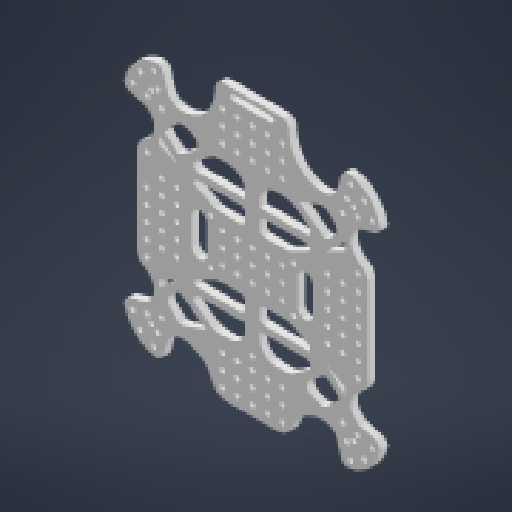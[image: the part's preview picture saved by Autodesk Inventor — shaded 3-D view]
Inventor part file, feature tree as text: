
AUTODESK INVENTOR PART (.ipt)
format: ipt  version: 2023 (Build 270158000, 158)  size: 962,048 bytes
history: native  units: mm
features: fillet x10, other x9, extrude x7, sketch x5, reference x4
ambient origin geometry x8: Origin, YZ Plane, XZ Plane, XY Plane, X Axis, Y Axis, Z Axis, Center Point
bodies: Solid1 (feature_tree)
feature tree (35):
  other  "Base Sketch With Dimensions"
  extrude  "Extrusion1"  TaperAngle=30.0deg  [1 undecoded]
  fillet  "Fillet1"  [1 undecoded]
  sketch  "Sketch3"  dims[d0=3.5mm d1=30.0deg d2=30.0deg]
  extrude  "Side Extensions"  TaperAngle=30.0deg  [1 undecoded]
  extrude  "Bottom Holes"  TaperAngle=30.0deg  [1 undecoded]
  fillet  "Fillet2"  Radius=45.0mm
  extrude  "ESC holders"  Depth=25.0mm
  extrude  "Hole Countersinks"  TaperAngle=135.0deg  [1 undecoded]
  extrude  "Skeleton"  TaperAngle=135.0deg  [1 undecoded]
  fillet  "Fillet3"  Radius=20.0mm
  fillet  "Fillet4"  Radius=120.0mm
  fillet  "Fillet5"  Radius=120.0mm
  fillet  "Fillet6"  Radius=25.0mm
  fillet  "Fillet8"  Radius=5.0mm
  fillet  "Fillet9"  Radius=5.0mm
  fillet  "Fillet10"  Radius=10.0mm
  fillet  "Fillet11"  Radius=10.0mm
  extrude  "Extrusion9"  Depth=10.0mm
  reference  "Reference1"
  reference  "Reference2"
  reference  "Reference3"
  reference  "Reference4"
  sketch  "Sketch4"  dims[d3=20.0mm d5=30.0deg d6=30.0deg]
  other  "Skeleton Sketch"
  sketch  "Sketch6"  dims[d9=30.0deg d10=30.0deg d13=30.0deg d14=30.0deg d16=45.0mm]
  sketch  "Sketch7"  dims[d17=140.0mm d18=25.0mm]
  sketch  "Sketch8"  dims[d19=70.0mm d23=135.0deg d25=135.0deg d29=20.0mm d30=120.0mm d32=120.0mm d40=25.0mm d41=5.0mm d44=5.0mm d45=0.0mm d46=10.0mm d80=50.0mm d82=10.0mm d83=30.0mm d85=10.0mm d88=50.0mm d90=10.0mm d91=30.0mm d93=10.0mm d97=5.0mm d98=50.0mm d102=10.0mm d103=0.0mm d104=17.5mm d105=0.0mm d106=70.0mm d107=10.0mm d108=50.0mm d109=30.0mm d134=3.5mm d135=0.5mm d136=0.5mm d137=30.0mm d138=30.0mm d139=25.0mm d140=0.0mm d151=6.5mm d152=50.0mm d154=10.0mm d155=30.0mm d157=10.0mm d160=30.0mm d162=10.0mm d163=50.0mm d165=10.0mm d168=50.0mm d170=10.0mm d171=30.0mm d173=10.0mm d176=30.0mm d178=10.0mm d179=50.0mm d181=10.0mm d184=50.0mm d186=10.0mm d187=30.0mm d189=10.0mm d192=2.0mm d193=0.0mm d204=5.0mm d205=5.0mm d206=5.0mm d207=5.0mm d208=2.0mm d209=0.0mm d210=5.0mm d211=5.0mm d212=5.0mm d213=2.0mm d214=10.0mm d216=5.0mm d217=5.0mm d218=5.0mm d220=5.0mm d221=10.0mm d222=15.0mm d223=5.0mm d225=5.0mm d227=10.0mm d228=3.0mm d229=50.0mm d230=30.0mm d232=10.0mm d233=50.0mm d235=10.0mm d238=3.5mm d239=100.0mm d240=5.0mm d241=5.0mm d242=5.0mm d243=3.0mm d244=4.0mm d246=25.0mm d247=10.0mm d248=5.0mm d249=15.0mm d250=15.0mm d252=3.5mm d253=27.5mm d254=27.5mm d255=85.0mm d256=10.0mm d257=0.0mm d258=140.0mm d259=0.0mm d260=0.0mm d261=0.0mm d262=0.872665mm]
  parser-record x1  (decoder bookkeeping rows leaked as tree rows — omitted from the tree; the rows remain in map.json)
  other  "total.iam"
  other  "_arm:3"
  other  "body holder:1"
  other  "_arm:4"
  other  "_arm:2"
  other  "_arm:1"
note: 6 required parameter values undecoded (feature->parameter linkage not recoverable at this tier; creation-order binding heuristic only, values carry confidence <= 0.55)
note: 1 file-system path scrubbed to <path> (originals preserved in map.json)
